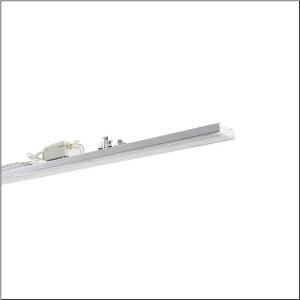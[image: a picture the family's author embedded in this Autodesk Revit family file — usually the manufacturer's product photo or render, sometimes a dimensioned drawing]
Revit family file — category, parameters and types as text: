
# Revit family: licross_r__21_recessed_ho_52te1emn4e5s_f825
name_source: partatom
category: Lighting Fixtures
units: mm (PartAtom-declared; Revit-internal decimal feet)

## family parameters
Cut with Voids When Loaded = No
Host = Face
Light Source = No
Part Type = Normal
Room Calculation Point = No
Round Connector Dimension = Use Diameter
Shared = No

## types (1)
- --- (1 x LED, 14710 lm, 83.1 W, 4000K)
    Apparent Load = 83 VA
    CIE Flux Codes = 85 95 99 100 100
    Color Rendering = 80
    Color Temperature = 4000K
    Default Elevation = 1800 mm
    Description = Licross® 21 Recessed HO, luminaire insert, of sheet steel, galvanised, coil coated, white, length: 1.500mm, width: 66mm, height: 67mm, LED rated luminous flux: 14.710lm, light colour: 840, control gear: ON/OFF Multilumen, with plug, 3-pole, with phase selection, mains connection: 220..240V, AC, 50/60Hz, rated input power: 83W, halogen-free wiring, primary light control with lens, of plastic, primary optical cover: cover, of PMMA, light emission: direct distribution, primary light characteristic: symmetric, protection rating (complete): IP54, insulation class (complete): insulation class I (protective earthing), certification: CE, ENEC, VDE, UKCA, protection symbol: D if used in an environment with non-conductive dust loads with corresponding accessories, impact resistance: IK06, permissible ambient temperature for indoor applications: -35..+30°C, corresponds to IFS (International Featured Standards) requirements for safety and quality in the food industry, reducing of maximum allowable ambient temperature of 5°C with ceiling mounting, LABS conformity tested according to VDMA 24364:2018-05, packaging unit: 1 piece
    Height = 58 mm
    Lamp = 1 x LED
    Lamp Light Flux = 14710 lm
    Lamp Power = 83.1 W
    Lamp count = 1
    Length = 1500 mm
    Luminous efficacy = 177 lm/W
    Manufacturer = Siteco
    ModVariant = No
    Model = 52TE1EMN4E5S
    Mounting Place = Ceiling
    Mounting Type = Pendant
    Number of Poles = 1
    OnlyDefault = Yes
    Power Factor = 1
    Product Name = Licross® 21 Recessed HO
    Product group = luminaire insert
    ProductGroupID = 901
    Protection Class = Protection class I
    Protection Degree = IP 54
    RLX_Detail_Level = 1
    RLX_Emergency_Light_Flux = 0 lm
    RLX_Emergency_Type = 0
    RLX_Emergency_Type_DB = No
    RlxData = <blob elided: 22357 chars, md5=c0be7e2e>
    Socket = socket
    Standby Power = 0 W
    System Light Flux = 14710 lm
    System Power = 83 W
    Type Comments = factory setting: luminous flux: 100 % | (A | C | E) | 195 mA
    Type Image = l_1296930.jpg
    URL = http://relux.com
    VarID = @adj_036605
    Voltage = 0 V
    Weight = 0.00 kg
    Width = 66 mm

## geometry (parser evidence)
native form markers: Blend x4, Sweep x9
no freeform markers — native parametric forms only
